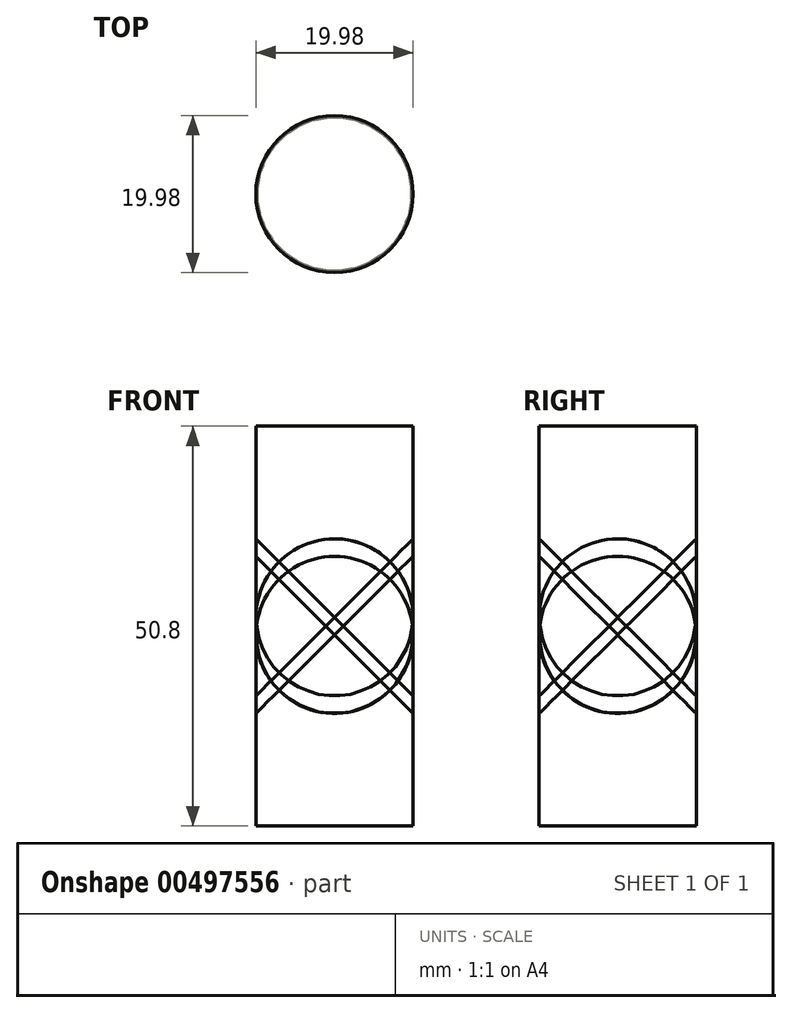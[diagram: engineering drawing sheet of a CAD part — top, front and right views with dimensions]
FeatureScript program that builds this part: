
annotation { "Feature Type Name" : "Feature", "Feature Type Description" : "" }
export const myFeature = defineFeature(function(context is Context, id is Id, definition is map)
    precondition{}
    {
        {
            var Q0;
            Q0=qCreatedBy(makeId("Top.planeOp"),FACE);
            var sketch = newSketch(context, id + "F0", { "sketchPlane" : qUnion([Q0])});
            skLineSegment(sketch, "E0.bottom", {"start": v(12.7, -12.7) * mm, "end": v(-12.7, -12.7) * mm});
            skLineSegment(sketch, "E0.top", {"start": v(12.7, 12.7) * mm, "end": v(-12.7, 12.7) * mm});
            skLineSegment(sketch, "E0.left", {"start": v(12.7, -12.7) * mm, "end": v(12.7, 12.7) * mm});
            skLineSegment(sketch, "E0.right", {"start": v(-12.7, -12.7) * mm, "end": v(-12.7, 12.7) * mm});
            skPoint(sketch, "E0.middle", {"position": v(0, 0) * mm});
            skSolve(sketch);
        }
        {
            var Q0;
            Q0=makeQuery(id+"F0.imprint","IMPRINT",FACE,{"disambiguationData":[TD([[makeQuery(id+"F0.imprint","IMPRINT",EDGE,{"derivedFrom":sQuery(id+"F0.wireOp",EDGE,"E0.bottom")}),-1.0]])]});
            extrude(context, id + "F1", {"entities" : qUnion([Q0]), "endBound" : BoundingType.SYMMETRIC, "depth" : 50.8 * mm});
        }
        {
            var Q0;
            Q0=qCreatedBy(makeId("Front.planeOp"),FACE);
            var sketch = newSketch(context, id + "F2", { "sketchPlane" : qUnion([Q0])});
            skLineSegment(sketch, "E1", {"start": v(12.7, 13.81) * mm, "end": v(-11.13, -10.01) * mm});
            skLineSegment(sketch, "E2", {"start": v(-11.13, -10.01) * mm, "end": v(-10.01, -11.13) * mm});
            skLineSegment(sketch, "E3", {"start": v(-10.01, -11.13) * mm, "end": v(13.81, 12.7) * mm});
            skLineSegment(sketch, "E4", {"start": v(13.81, 12.7) * mm, "end": v(12.7, 13.81) * mm});
            skLineSegment(sketch, "E5", {"start": v(-10.57, -10.57) * mm, "end": v(13.26, 13.26) * mm, "construction": true});
            skLineSegment(sketch, "E6", {"start": v(-11.13, -10.01) * mm, "end": v(-12.7, -10.01) * mm, "construction": true});
            skSolve(sketch);
        }
        {
            var Q0;
            Q0 = qSketchRegion(id + "F2", true);
            var Q1;
            Q1=makeQuery(id+"F1.opExtrude","SWEPT_FACE",FACE,{"disambiguationData":[OSD([sQuery(id+"F0.wireOp",EDGE,"E0.bottom")])]});
            extrude(context, id + "F3", {"entities" : qUnion([Q0]), "endBound" : BoundingType.SYMMETRIC, "endBoundEntityFace" : qUnion([Q1]), "depth" : 25.4 * mm, "hasSecondDirection" : true, "secondDirectionBound" : SecondDirectionBoundingType.UP_TO_NEXT, "secondDirectionOppositeDirection" : true, "secondDirectionDepth" : 25.4 * mm});
        }
        {
            var Q0;
            Q0=qCreatedBy(makeId("Front.planeOp"),FACE);
            var sketch = newSketch(context, id + "F4", { "sketchPlane" : qUnion([Q0])});
            skLineSegment(sketch, "E7", {"start": v(0, 0) * mm, "end": v(0, 53.24) * mm});
            skSolve(sketch);
        }
        {
            var Q0;
            Q0=makeQuery(id+"F3.opExtrude","SWEPT_BODY",BODY,{"disambiguationData":[OSD([sQuery(id+"F2.wireOp",EDGE,"E1"),sQuery(id+"F2.wireOp",EDGE,"E2"),sQuery(id+"F2.wireOp",EDGE,"E3"),sQuery(id+"F2.wireOp",EDGE,"E4")])]});
            var Q1;
            Q1=sQuery(id+"F4.wireOp",EDGE,"E7");
            circularPattern(context, id + "F5", {"entities" : qUnion([Q0]), "axis" : qUnion([Q1]), "angle" : 360 * degree, "instanceCount" : 4, "equalSpace" : true});
        }
        {
            var Q0;
            Q0=qCreatedBy(makeId("Top.planeOp"),FACE);
            var sketch = newSketch(context, id + "F6", { "sketchPlane" : qUnion([Q0])});
            skCircle(sketch, "E8", {"center": v(0, 0) * mm, "radius": 10.01 * mm});
            skCircle(sketch, "E9", {"center": v(0, 0) * mm, "radius": 20.18 * mm});
            skSolve(sketch);
        }
        {
            var Q0;
            Q0 = qSketchRegion(id + "F6", true);
            extrude(context, id + "F7", {"entities" : qUnion([Q0]), "operationType" : NewBodyOperationType.REMOVE, "endBound" : BoundingType.THROUGH_ALL, "depth" : 25.4 * mm, "hasSecondDirection" : true, "secondDirectionBound" : SecondDirectionBoundingType.THROUGH_ALL, "secondDirectionOppositeDirection" : true, "secondDirectionDepth" : 25.4 * mm});
        }
        {
            var Q0;
            Q0=makeQuery(id+"F1.opExtrude","CAP_FACE",FACE,{"disambiguationData":[OSD([sQuery(id+"F0.wireOp",EDGE,"E0.bottom"),sQuery(id+"F0.wireOp",EDGE,"E0.top"),sQuery(id+"F0.wireOp",EDGE,"E0.left"),sQuery(id+"F0.wireOp",EDGE,"E0.right")])],"isStart":false});
            var sketch = newSketch(context, id + "F8", { "sketchPlane" : qUnion([Q0])});
            skCircle(sketch, "E10", {"center": v(0, 0) * mm, "radius": 9.99 * mm});
            skCircle(sketch, "E11", {"center": v(0, 0) * mm, "radius": 27.67 * mm});
            skSolve(sketch);
        }
        {
            var Q0;
            Q0 = qSketchRegion(id + "F8", true);
            extrude(context, id + "F9", {"entities" : qUnion([Q0]), "operationType" : NewBodyOperationType.REMOVE, "endBound" : BoundingType.THROUGH_ALL, "oppositeDirection" : true, "depth" : 25.4 * mm});
        }
    });
